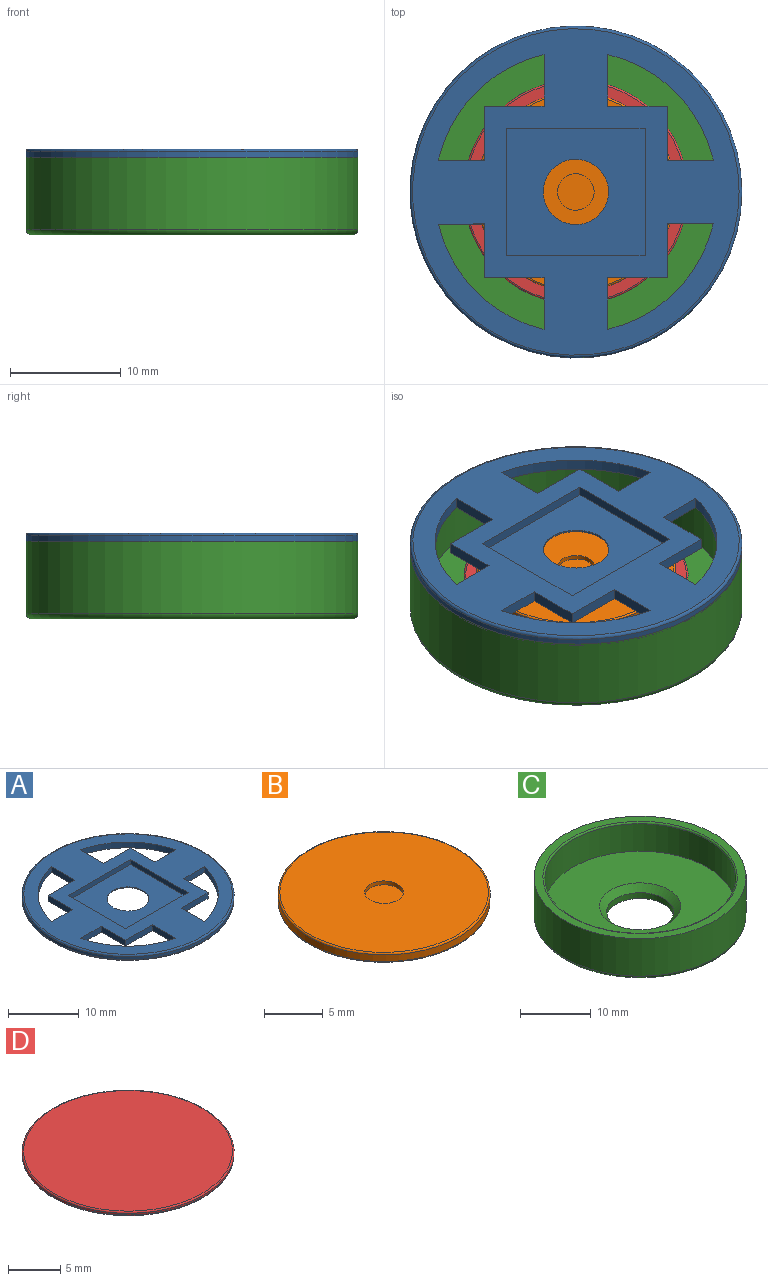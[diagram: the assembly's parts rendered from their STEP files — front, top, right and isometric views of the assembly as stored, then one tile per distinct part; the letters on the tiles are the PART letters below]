
ASSEMBLY  parts=4 mates=3
PART A: 31 faces, bbox 32.5x32.5x1 mm
  f0: cylinder r=15mm len=30mm, axis (0,0,-1), area 47.1mm2, adj f9,f10
  f1: plane 29.5x29.5mm, normal (0,0,1), area 391.7mm2, adj f3,f4,f5,f6,f10,f11,f12,f13
  f2: plane 29.5x29.5mm, normal (0,0,-1), area 508.1mm2, adj f8,f9,f11,f12,f13,f14,f15,f16
  f3: plane 11.5x0.85mm, normal (1,0,0), area 9.8mm2, adj f1,f4,f6,f7
  f4: plane 12.5x0.85mm, normal (0,1,0), area 10.6mm2, adj f1,f3,f5,f7
  f5: plane 11.5x0.85mm, normal (-1,0,0), area 9.8mm2, adj f1,f4,f6,f7
  f6: plane 12.5x0.85mm, normal (0,-1,0), area 10.6mm2, adj f1,f3,f5,f7
  f7: plane 12.5x11.5mm, normal (0,0,1), area 116.4mm2, adj f3,f4,f5,f6,f8
  f8: cylinder r=2.95mm len=5.9mm, axis (0,0,1), area 2.8mm2, adj f2,f7
  f9: torus R=14.75mm, axis (0,0,1), area 36.8mm2, adj f0,f2
  f10: torus R=14.75mm, axis (0,0,1), area 36.8mm2, adj f0,f1
  f11: cylinder r=12.75mm len=9.54mm, axis (0,0,1), area 14.2mm2, adj f1,f2,f12,f13
  f12: plane 4.67x1mm, normal (-1,0,0), area 4.7mm2, adj f1,f2,f11,f14
  f13: plane 4.16x1mm, normal (0,-1,0), area 4.2mm2, adj f1,f2,f11,f15
  f14: plane 5.38x1mm, normal (0,-1,0), area 5.4mm2, adj f1,f2,f12,f15
  f15: plane 4.86x1mm, normal (-1,0,0), area 4.9mm2, adj f1,f2,f13,f14
  f16: cylinder r=12.75mm len=9.54mm, axis (0,0,1), area 14.2mm2, adj f1,f2,f17,f18
  f17: plane 4.17x1mm, normal (0,-1,0), area 4.2mm2, adj f1,f2,f16,f19
  f18: plane 4.67x1mm, normal (1,0,0), area 4.7mm2, adj f1,f2,f16,f20
  f19: plane 4.86x1mm, normal (1,0,0), area 4.9mm2, adj f1,f2,f17,f20
  f20: plane 5.38x1mm, normal (0,-1,0), area 5.4mm2, adj f1,f2,f18,f19
  f21: plane 5.38x1mm, normal (0,1,0), area 5.4mm2, adj f1,f2,f22,f24
  f22: plane 4.88x1mm, normal (1,0,0), area 4.9mm2, adj f1,f2,f21,f23
  f23: plane 4.17x1mm, normal (0,1,0), area 4.2mm2, adj f1,f2,f22,f25
  f24: plane 4.67x1mm, normal (1,0,0), area 4.7mm2, adj f1,f2,f21,f25
  f25: cylinder r=12.75mm len=9.55mm, axis (0,0,1), area 14.2mm2, adj f1,f2,f23,f24
  f26: cylinder r=12.75mm len=9.55mm, axis (0,0,1), area 14.2mm2, adj f1,f2,f27,f29
  f27: plane 4.17x1mm, normal (0,1,0), area 4.2mm2, adj f1,f2,f26,f28
  f28: plane 4.88x1mm, normal (-1,0,0), area 4.9mm2, adj f1,f2,f27,f30
  f29: plane 4.67x1mm, normal (-1,0,0), area 4.7mm2, adj f1,f2,f26,f30
  f30: plane 5.38x1mm, normal (0,1,0), area 5.4mm2, adj f1,f2,f28,f29
PART B: 7 faces, bbox 19.5x19.5x1 mm
  f0: cylinder r=9mm len=18mm, axis (0,0,-1), area 39.6mm2, adj f3,f4
  f1: plane 17.7x17.7mm, normal (0,0,1), area 237.5mm2, adj f4,f5
  f2: plane 17.7x17.7mm, normal (0,0,-1), area 246.1mm2, adj f3
  f3: torus R=8.85mm, axis (0,0,1), area 13.2mm2, adj f0,f2
  f4: torus R=8.85mm, axis (0,0,1), area 13.2mm2, adj f0,f1
  f5: cylinder r=1.65mm len=3.3mm, axis (0,0,1), area 4.1mm2, adj f1,f6
  f6: plane 3.3x3.3mm, normal (0,0,1), area 8.6mm2, adj f5
PART C: 9 faces, bbox 32.5x32.5x7 mm
  f0: cylinder r=15mm len=30mm, axis (0,0,-1), area 612.6mm2, adj f1,f6
  f1: plane 30x30mm, normal (0,0,1), area 112.9mm2, adj f0,f5
  f2: plane 29x29mm, normal (0,0,-1), area 589.6mm2, adj f6,f7
  f3: cylinder r=13.5mm len=27mm, axis (0,0,1), area 402.9mm2, adj f4,f5
  f4: plane 27x27mm, normal (0,0,1), area 468.7mm2, adj f3,f8
  f5: torus R=13.75mm, axis (0,0,1), area 33.5mm2, adj f1,f3
  f6: torus R=14.5mm, axis (0,0,1), area 73.1mm2, adj f0,f2
  f7: cylinder r=4.75mm len=9.5mm, axis (0,0,1), area 29.8mm2, adj f2,f8
  f8: cone r=4.75mm half-angle=45deg, axis (0,0,1), area 46.7mm2, adj f4,f7
PART D: 5 faces, bbox 21.9x21.9x0.5 mm
  f0: cylinder r=10.12mm len=20.25mm, axis (0,0,-1), area 12.7mm2, adj f3,f4
  f1: plane 19.95x19.95mm, normal (0,0,1), area 312.6mm2, adj f4
  f2: plane 19.95x19.95mm, normal (0,0,-1), area 312.6mm2, adj f3
  f3: torus R=9.97mm, axis (0,0,1), area 14.9mm2, adj f0,f2
  f4: torus R=9.97mm, axis (0,0,1), area 14.9mm2, adj f0,f1
PLACE A t=(-0.69,-1.33,5.26)mm
PLACE B t=(-0.69,-1.33,2.54)mm
PLACE C t=(-0.69,-1.33,-1.49)mm fixed
PLACE D t=(-0.69,-1.33,2.04)mm
MATE fastened D.f0 <-> B.f0  axis (0,0,1) through (-0.69,-1.33,2.54)mm
MATE fastened A.f0 <-> C.f0  axis (0,0,1) through (-0.69,-1.33,5.51)mm
MATE slider D.f0 <-> C.f3  axis (0,0,-1) through (-0.69,-1.33,2.04)mm
